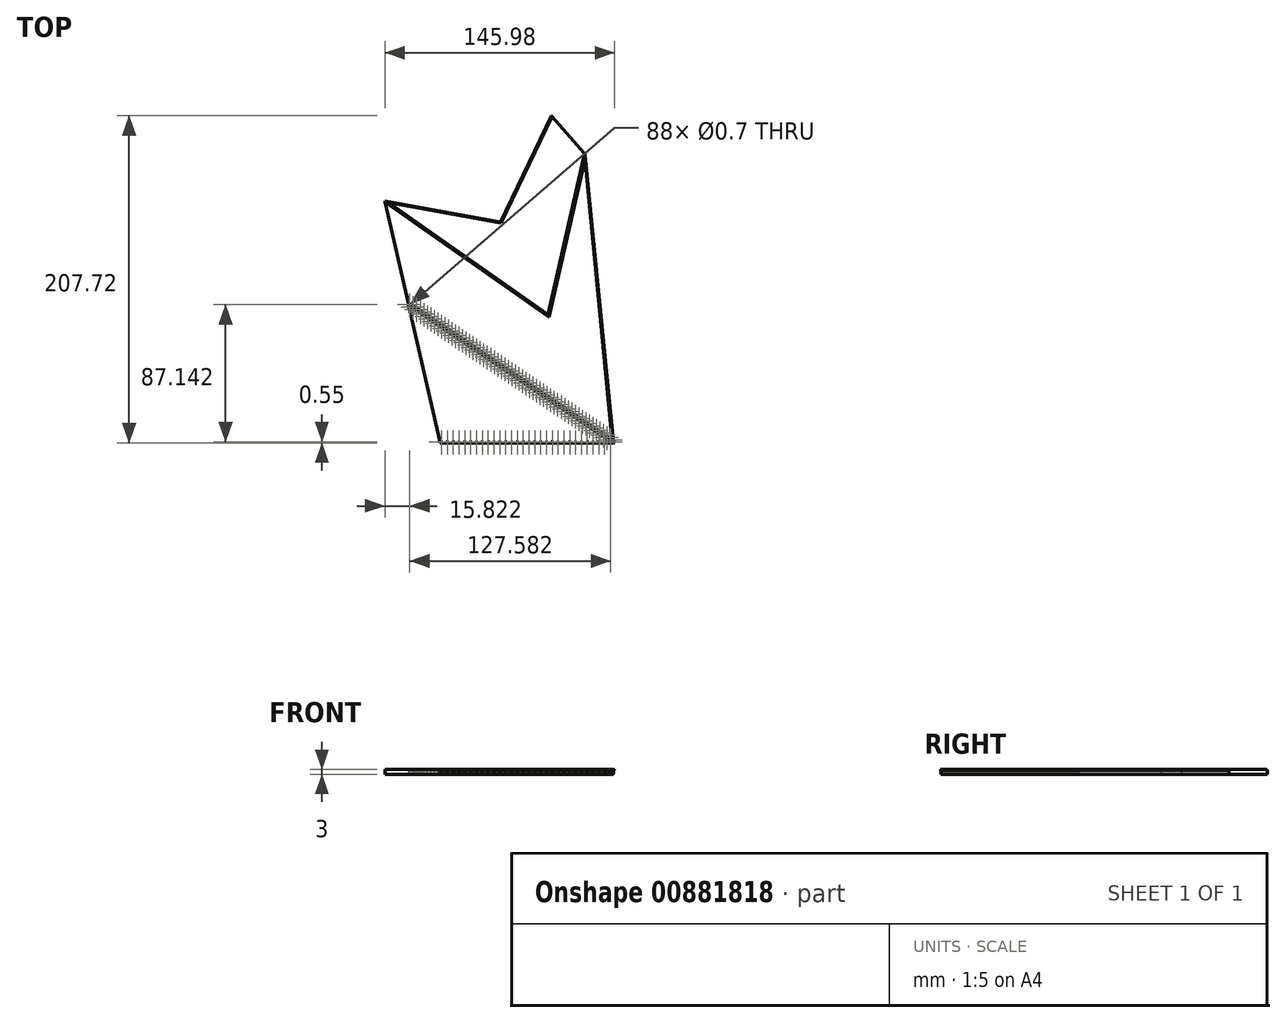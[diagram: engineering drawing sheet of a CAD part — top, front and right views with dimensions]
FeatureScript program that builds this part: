
annotation { "Feature Type Name" : "Feature", "Feature Type Description" : "" }
export const myFeature = defineFeature(function(context is Context, id is Id, definition is map)
    precondition{}
    {
        {
            var Q0;
            Q0=qCreatedBy(makeId("Top.planeOp"),FACE);
            var sketch = newSketch(context, id + "F0", { "sketchPlane" : qUnion([Q0])});
            skLineSegment(sketch, "E0", {"start": v(0, 0) * mm, "end": v(110, 0) * mm});
            skLineSegment(sketch, "E1", {"start": v(0, 0) * mm, "end": v(-20.1, 87.72) * mm});
            skLineSegment(sketch, "E2", {"start": v(-20.1, 87.72) * mm, "end": v(110, 0) * mm});
            skLineSegment(sketch, "E3", {"start": v(110, 0) * mm, "end": v(68.99, 80.11) * mm});
            skLineSegment(sketch, "E4", {"start": v(68.99, 80.11) * mm, "end": v(-20.1, 87.72) * mm});
            skLineSegment(sketch, "E5", {"start": v(-20.1, 87.72) * mm, "end": v(-35.08, 153.03) * mm});
            skLineSegment(sketch, "E6", {"start": v(-35.08, 153.03) * mm, "end": v(68.99, 80.11) * mm});
            skLineSegment(sketch, "E7", {"start": v(68.99, 80.11) * mm, "end": v(38.45, 139.75) * mm});
            skLineSegment(sketch, "E8", {"start": v(38.45, 139.75) * mm, "end": v(-35.08, 153.03) * mm});
            skPoint(sketch, "E9.center", {"position": v(55, -75.7) * mm});
            skLineSegment(sketch, "E10", {"start": v(68.99, 80.11) * mm, "end": v(97.55, 127.85) * mm});
            skLineSegment(sketch, "E11", {"start": v(38.45, 139.75) * mm, "end": v(70.67, 207.17) * mm});
            skLineSegment(sketch, "E12.MirrorCS", {"start": v(92.22, 182.65) * mm, "end": v(70.67, 207.17) * mm});
            skLineSegment(sketch, "E13", {"start": v(92.22, 182.65) * mm, "end": v(89.24, 213.26) * mm});
            skLineSegment(sketch, "E14", {"start": v(89.24, 213.26) * mm, "end": v(70.67, 207.17) * mm});
            skLineSegment(sketch, "E15", {"start": v(92.22, 182.65) * mm, "end": v(110, 0) * mm});
            skLineSegment(sketch, "E16", {"start": v(68.99, 80.11) * mm, "end": v(70.67, 207.17) * mm});
            skLineSegment(sketch, "E17", {"start": v(68.99, 80.11) * mm, "end": v(92.22, 182.65) * mm});
            skLineSegment(sketch, "E18", {"start": v(55, -75.7) * mm, "end": v(0, 0) * mm});
            skLineSegment(sketch, "E19", {"start": v(55, -75.7) * mm, "end": v(110, 0) * mm});
            skLineSegment(sketch, "E20", {"start": v(-20.1, 87.72) * mm, "end": v(-18.6, 105.36) * mm, "construction": true});
            skLineSegment(sketch, "E21", {"start": v(-18.6, 105.36) * mm, "end": v(-5.6, 104.24) * mm, "construction": true});
            skLineSegment(sketch, "E22", {"start": v(-20.1, 87.72) * mm, "end": v(-11.2, 100.93) * mm, "construction": true});
            skLineSegment(sketch, "E23", {"start": v(-11.2, 100.93) * mm, "end": v(-3.63, 95.82) * mm, "construction": true});
            skSolve(sketch);
        }
        {
            var Q0;
            Q0=qCreatedBy(makeId("Right.planeOp"),FACE);
            var sketch = newSketch(context, id + "F1", { "sketchPlane" : qUnion([Q0])});
            skLineSegment(sketch, "E24", {"start": v(0.55, 0) * mm, "end": v(-0.55, 0) * mm});
            skArc(sketch, "E25.MirrorCS", {"start": v(0.55, 0) * mm, "mid": v(0, -0.55) * mm, "end": v(-0.55, 0) * mm});
            skSolve(sketch);
        }
        {
            var Q0;
            Q0=makeQuery(id+"F1.imprint","IMPRINT",FACE,{"disambiguationData":[TD([[makeQuery(id+"F1.imprint","IMPRINT",EDGE,{"derivedFrom":sQuery(id+"F1.wireOp",EDGE,"E24")}),1.0]])]});
            var Q1;
            Q1=sQuery(id+"F0.wireOp",EDGE,"E0");
            var Q2;
            Q2=sQuery(id+"F0.wireOp",EDGE,"E3");
            var Q3;
            Q3=sQuery(id+"F0.wireOp",EDGE,"E7");
            sweep(context, id + "F2", {"profiles" : qUnion([Q0]), "path" : qUnion([Q1, Q2, Q3])});
        }
        {
            var Q0;
            Q0=sQuery(id+"F0.wireOp",EDGE,"E21");
            var Q1;
            Q1=sQuery(id+"F0.wireOp",VERTEX,"E1.end");
            cPlane(context, id + "F3", {"entities" : qUnion([Q0, Q1]), "cplaneType" : CPlaneType.LINE_POINT, "offset" : 25 * mm, "width" : 150 * mm, "height" : 150 * mm});
        }
        {
            var Q0;
            Q0=makeQuery(id+"F0.imprint","IMPRINT",FACE,{"disambiguationData":[TD([[makeQuery(id+"F0.imprint","IMPRINT",EDGE,{"derivedFrom":sQuery(id+"F0.wireOp",EDGE,"E0")}),-1.0]])]});
            var Q1;
            Q1=makeQuery(id+"F0.imprint","IMPRINT",FACE,{"disambiguationData":[TD([[makeQuery(id+"F0.imprint","IMPRINT",EDGE,{"derivedFrom":sQuery(id+"F0.wireOp",EDGE,"E1")}),-1.0]])]});
            var Q2;
            Q2=makeQuery(id+"F0.imprint","IMPRINT",FACE,{"disambiguationData":[TD([[makeQuery(id+"F0.imprint","IMPRINT",EDGE,{"derivedFrom":sQuery(id+"F0.wireOp",EDGE,"E2")}),1.0]])]});
            var Q3;
            Q3=makeQuery(id+"F0.imprint","IMPRINT",FACE,{"disambiguationData":[TD([[makeQuery(id+"F0.imprint","IMPRINT",EDGE,{"derivedFrom":sQuery(id+"F0.wireOp",EDGE,"E4")}),-1.0]])]});
            var Q4;
            Q4=makeQuery(id+"F0.imprint","IMPRINT",FACE,{"disambiguationData":[TD([[makeQuery(id+"F0.imprint","IMPRINT",EDGE,{"derivedFrom":sQuery(id+"F0.wireOp",EDGE,"E6")}),1.0]])]});
            var Q5;
            Q5=makeQuery(id+"F0.imprint","IMPRINT",FACE,{"disambiguationData":[TD([[makeQuery(id+"F0.imprint","IMPRINT",EDGE,{"derivedFrom":sQuery(id+"F0.wireOp",EDGE,"E7")}),-1.0]])]});
            var Q6;
            Q6=makeQuery(id+"F0.imprint","IMPRINT",FACE,{"disambiguationData":[TD([[makeQuery(id+"F0.imprint","IMPRINT",EDGE,{"derivedFrom":sQuery(id+"F0.wireOp",EDGE,"E12.MirrorCS")}),1.0]])]});
            var Q7;
            {var subQ0=sQuery(id+"F0.wireOp",EDGE,"E10");Q7=makeQuery(id+"F0.imprint","IMPRINT",FACE,{"disambiguationData":[TD([[makeQuery(id+"F0.imprint","IMPRINT",EDGE,{"derivedFrom":subQ0}),1.0]])]});}
            var Q8;
            {var subQ0=sQuery(id+"F0.wireOp",EDGE,"E3");Q8=makeQuery(id+"F0.imprint","IMPRINT",FACE,{"disambiguationData":[TD([[makeQuery(id+"F0.imprint","IMPRINT",EDGE,{"derivedFrom":subQ0}),-1.0]])]});}
            extrude(context, id + "F4", {"entities" : qUnion([Q0, Q1, Q2, Q3, Q4, Q5, Q6, Q7, Q8]), "operationType" : NewBodyOperationType.ADD, "oppositeDirection" : true, "depth" : 3 * mm, "offsetDistance" : 25 * mm});
        }
        {
            var Q0;
            Q0=sQuery(id+"F0.wireOp",EDGE,"E23");
            var Q1;
            Q1=sQuery(id+"F0.wireOp",VERTEX,"E1.end");
            cPlane(context, id + "F5", {"entities" : qUnion([Q0, Q1]), "cplaneType" : CPlaneType.LINE_POINT, "offset" : 25 * mm, "width" : 150 * mm, "height" : 150 * mm});
        }
        {
            var Q0;
            Q0=qCreatedBy(id+"F5.planeOp",FACE);
            var sketch = newSketch(context, id + "F6", { "sketchPlane" : qUnion([Q0])});
            skArc(sketch, "E26", {"start": v(60.94, 0) * mm, "mid": v(61.5, -0.55) * mm, "end": v(62.04, 0) * mm});
            skLineSegment(sketch, "E27", {"start": v(62.04, 0) * mm, "end": v(60.94, 0) * mm});
            skArc(sketch, "E28.MirrorCS", {"start": v(60.94, 0) * mm, "mid": v(61.5, 0.55) * mm, "end": v(62.04, 0) * mm});
            skSolve(sketch);
        }
        {
            var Q0;
            Q0=makeQuery(id+"F6.imprint","IMPRINT",FACE,{"disambiguationData":[TD([[makeQuery(id+"F6.imprint","IMPRINT",EDGE,{"derivedFrom":sQuery(id+"F6.wireOp",EDGE,"E26")}),1.0]])]});
            var Q1;
            Q1=sQuery(id+"F0.wireOp",EDGE,"E2");
            var Q2;
            Q2=sQuery(id+"F0.wireOp",EDGE,"E15");
            var Q3;
            Q3=sQuery(id+"F0.wireOp",EDGE,"E17");
            var Q4;
            Q4=sQuery(id+"F0.wireOp",EDGE,"E6");
            var Q5;
            Q5=sQuery(id+"F0.wireOp",EDGE,"E8");
            var Q6;
            Q6=sQuery(id+"F0.wireOp",EDGE,"E11");
            sweep(context, id + "F7", {"operationType" : NewBodyOperationType.REMOVE, "profiles" : qUnion([Q0]), "path" : qUnion([Q1, Q2, Q3, Q4, Q5, Q6])});
        }
        {
            var Q0;
            Q0=makeQuery(id+"F6.imprint","IMPRINT",FACE,{"disambiguationData":[TD([[makeQuery(id+"F6.imprint","IMPRINT",EDGE,{"derivedFrom":sQuery(id+"F6.wireOp",EDGE,"E27")}),-1.0]])]});
            var Q1;
            Q1=sQuery(id+"F0.wireOp",EDGE,"E2");
            sweep(context, id + "F8", {"operationType" : NewBodyOperationType.REMOVE, "profiles" : qUnion([Q0]), "path" : qUnion([Q1])});
        }
        {
            var Q0;
            Q0=qCreatedBy(makeId("Top.planeOp"),FACE);
            var sketch = newSketch(context, id + "F9", { "sketchPlane" : qUnion([Q0])});
            skCircle(sketch, "E29", {"center": v(0.99, 0) * mm, "radius": 0.35 * mm});
            skCircle(sketch, "E30.2.0.0", {"center": v(216.79, 0) * mm, "radius": 0.35 * mm});
            skCircle(sketch, "E30.3.0.0", {"center": v(324.69, 0) * mm, "radius": 0.35 * mm});
            skCircle(sketch, "E30.4.0.0", {"center": v(432.59, 0) * mm, "radius": 0.35 * mm});
            skCircle(sketch, "E31.1.0.0", {"center": v(4.69, 0) * mm, "radius": 0.35 * mm});
            skCircle(sketch, "E31.2.0.0", {"center": v(8.39, 0) * mm, "radius": 0.35 * mm});
            skCircle(sketch, "E31.3.0.0", {"center": v(12.09, 0) * mm, "radius": 0.35 * mm});
            skCircle(sketch, "E31.4.0.0", {"center": v(15.79, 0) * mm, "radius": 0.35 * mm});
            skCircle(sketch, "E31.5.0.0", {"center": v(19.49, 0) * mm, "radius": 0.35 * mm});
            skCircle(sketch, "E31.6.0.0", {"center": v(23.19, 0) * mm, "radius": 0.35 * mm});
            skCircle(sketch, "E31.7.0.0", {"center": v(26.89, 0) * mm, "radius": 0.35 * mm});
            skCircle(sketch, "E31.8.0.0", {"center": v(30.59, 0) * mm, "radius": 0.35 * mm});
            skCircle(sketch, "E31.9.0.0", {"center": v(34.29, 0) * mm, "radius": 0.35 * mm});
            skCircle(sketch, "E31.10.0.0", {"center": v(37.99, 0) * mm, "radius": 0.35 * mm});
            skCircle(sketch, "E31.11.0.0", {"center": v(41.69, 0) * mm, "radius": 0.35 * mm});
            skCircle(sketch, "E31.12.0.0", {"center": v(45.39, 0) * mm, "radius": 0.35 * mm});
            skCircle(sketch, "E31.13.0.0", {"center": v(49.09, 0) * mm, "radius": 0.35 * mm});
            skCircle(sketch, "E31.14.0.0", {"center": v(52.79, 0) * mm, "radius": 0.35 * mm});
            skCircle(sketch, "E31.15.0.0", {"center": v(56.49, 0) * mm, "radius": 0.35 * mm});
            skCircle(sketch, "E31.16.0.0", {"center": v(60.19, 0) * mm, "radius": 0.35 * mm});
            skCircle(sketch, "E31.17.0.0", {"center": v(63.89, 0) * mm, "radius": 0.35 * mm});
            skCircle(sketch, "E31.18.0.0", {"center": v(67.59, 0) * mm, "radius": 0.35 * mm});
            skCircle(sketch, "E31.19.0.0", {"center": v(71.29, 0) * mm, "radius": 0.35 * mm});
            skCircle(sketch, "E31.20.0.0", {"center": v(74.99, 0) * mm, "radius": 0.35 * mm});
            skCircle(sketch, "E31.21.0.0", {"center": v(78.69, 0) * mm, "radius": 0.35 * mm});
            skCircle(sketch, "E31.22.0.0", {"center": v(82.39, 0) * mm, "radius": 0.35 * mm});
            skCircle(sketch, "E31.23.0.0", {"center": v(86.09, 0) * mm, "radius": 0.35 * mm});
            skCircle(sketch, "E31.24.0.0", {"center": v(89.79, 0) * mm, "radius": 0.35 * mm});
            skCircle(sketch, "E31.25.0.0", {"center": v(93.49, 0) * mm, "radius": 0.35 * mm});
            skCircle(sketch, "E31.26.0.0", {"center": v(97.19, 0) * mm, "radius": 0.35 * mm});
            skCircle(sketch, "E31.27.0.0", {"center": v(100.89, 0) * mm, "radius": 0.35 * mm});
            skCircle(sketch, "E31.28.0.0", {"center": v(104.59, 0) * mm, "radius": 0.35 * mm});
            skCircle(sketch, "E31.29.0.0", {"center": v(108.29, 0) * mm, "radius": 0.35 * mm});
            skLineSegment(sketch, "E31.direction1", {"start": v(0.99, 0) * mm, "end": v(4.69, 0) * mm, "construction": true});
            skCircle(sketch, "E32", {"center": v(-19.26, 87.14) * mm, "radius": 0.35 * mm});
            skCircle(sketch, "E33.1.0.0", {"center": v(-17.02, 85.63) * mm, "radius": 0.35 * mm});
            skCircle(sketch, "E33.2.0.0", {"center": v(-14.78, 84.13) * mm, "radius": 0.35 * mm});
            skCircle(sketch, "E33.3.0.0", {"center": v(-12.54, 82.62) * mm, "radius": 0.35 * mm});
            skCircle(sketch, "E33.4.0.0", {"center": v(-10.3, 81.11) * mm, "radius": 0.35 * mm});
            skCircle(sketch, "E33.5.0.0", {"center": v(-8.07, 79.6) * mm, "radius": 0.35 * mm});
            skCircle(sketch, "E33.6.0.0", {"center": v(-5.83, 78.1) * mm, "radius": 0.35 * mm});
            skCircle(sketch, "E33.7.0.0", {"center": v(-3.59, 76.59) * mm, "radius": 0.35 * mm});
            skCircle(sketch, "E33.8.0.0", {"center": v(-1.35, 75.08) * mm, "radius": 0.35 * mm});
            skCircle(sketch, "E33.9.0.0", {"center": v(0.89, 73.57) * mm, "radius": 0.35 * mm});
            skCircle(sketch, "E33.10.0.0", {"center": v(3.13, 72.07) * mm, "radius": 0.35 * mm});
            skCircle(sketch, "E33.11.0.0", {"center": v(5.36, 70.56) * mm, "radius": 0.35 * mm});
            skCircle(sketch, "E33.12.0.0", {"center": v(7.6, 69.05) * mm, "radius": 0.35 * mm});
            skCircle(sketch, "E33.13.0.0", {"center": v(9.84, 67.54) * mm, "radius": 0.35 * mm});
            skCircle(sketch, "E33.14.0.0", {"center": v(12.08, 66.04) * mm, "radius": 0.35 * mm});
            skCircle(sketch, "E33.15.0.0", {"center": v(14.32, 64.53) * mm, "radius": 0.35 * mm});
            skCircle(sketch, "E33.16.0.0", {"center": v(16.56, 63.02) * mm, "radius": 0.35 * mm});
            skCircle(sketch, "E33.17.0.0", {"center": v(18.8, 61.51) * mm, "radius": 0.35 * mm});
            skCircle(sketch, "E33.18.0.0", {"center": v(21.03, 60) * mm, "radius": 0.35 * mm});
            skCircle(sketch, "E33.19.0.0", {"center": v(23.27, 58.5) * mm, "radius": 0.35 * mm});
            skCircle(sketch, "E33.20.0.0", {"center": v(25.5, 57) * mm, "radius": 0.35 * mm});
            skCircle(sketch, "E33.21.0.0", {"center": v(27.75, 55.48) * mm, "radius": 0.35 * mm});
            skCircle(sketch, "E33.22.0.0", {"center": v(29.98, 53.98) * mm, "radius": 0.35 * mm});
            skCircle(sketch, "E33.23.0.0", {"center": v(32.22, 52.47) * mm, "radius": 0.35 * mm});
            skCircle(sketch, "E33.24.0.0", {"center": v(34.46, 50.96) * mm, "radius": 0.35 * mm});
            skCircle(sketch, "E33.25.0.0", {"center": v(36.7, 49.45) * mm, "radius": 0.35 * mm});
            skCircle(sketch, "E33.26.0.0", {"center": v(38.94, 47.95) * mm, "radius": 0.35 * mm});
            skCircle(sketch, "E33.27.0.0", {"center": v(41.18, 46.44) * mm, "radius": 0.35 * mm});
            skCircle(sketch, "E33.28.0.0", {"center": v(43.41, 44.93) * mm, "radius": 0.35 * mm});
            skCircle(sketch, "E33.29.0.0", {"center": v(45.65, 43.42) * mm, "radius": 0.35 * mm});
            skCircle(sketch, "E33.30.0.0", {"center": v(47.9, 41.91) * mm, "radius": 0.35 * mm});
            skCircle(sketch, "E33.31.0.0", {"center": v(50.13, 40.4) * mm, "radius": 0.35 * mm});
            skCircle(sketch, "E33.32.0.0", {"center": v(52.37, 38.9) * mm, "radius": 0.35 * mm});
            skCircle(sketch, "E33.33.0.0", {"center": v(54.6, 37.4) * mm, "radius": 0.35 * mm});
            skCircle(sketch, "E33.34.0.0", {"center": v(56.84, 35.88) * mm, "radius": 0.35 * mm});
            skCircle(sketch, "E33.35.0.0", {"center": v(59.08, 34.38) * mm, "radius": 0.35 * mm});
            skCircle(sketch, "E33.36.0.0", {"center": v(61.32, 32.87) * mm, "radius": 0.35 * mm});
            skCircle(sketch, "E33.37.0.0", {"center": v(63.56, 31.36) * mm, "radius": 0.35 * mm});
            skCircle(sketch, "E33.38.0.0", {"center": v(65.8, 29.85) * mm, "radius": 0.35 * mm});
            skCircle(sketch, "E33.39.0.0", {"center": v(68.04, 28.35) * mm, "radius": 0.35 * mm});
            skCircle(sketch, "E33.40.0.0", {"center": v(70.27, 26.84) * mm, "radius": 0.35 * mm});
            skCircle(sketch, "E33.41.0.0", {"center": v(72.51, 25.33) * mm, "radius": 0.35 * mm});
            skCircle(sketch, "E33.42.0.0", {"center": v(74.75, 23.82) * mm, "radius": 0.35 * mm});
            skCircle(sketch, "E33.43.0.0", {"center": v(76.99, 22.32) * mm, "radius": 0.35 * mm});
            skCircle(sketch, "E33.44.0.0", {"center": v(79.23, 20.8) * mm, "radius": 0.35 * mm});
            skCircle(sketch, "E33.45.0.0", {"center": v(81.47, 19.3) * mm, "radius": 0.35 * mm});
            skCircle(sketch, "E33.46.0.0", {"center": v(83.7, 17.8) * mm, "radius": 0.35 * mm});
            skCircle(sketch, "E33.47.0.0", {"center": v(85.94, 16.29) * mm, "radius": 0.35 * mm});
            skCircle(sketch, "E33.48.0.0", {"center": v(88.18, 14.78) * mm, "radius": 0.35 * mm});
            skCircle(sketch, "E33.49.0.0", {"center": v(90.42, 13.27) * mm, "radius": 0.35 * mm});
            skCircle(sketch, "E33.50.0.0", {"center": v(92.66, 11.76) * mm, "radius": 0.35 * mm});
            skCircle(sketch, "E33.51.0.0", {"center": v(94.9, 10.26) * mm, "radius": 0.35 * mm});
            skCircle(sketch, "E33.52.0.0", {"center": v(97.13, 8.75) * mm, "radius": 0.35 * mm});
            skCircle(sketch, "E33.53.0.0", {"center": v(99.37, 7.24) * mm, "radius": 0.35 * mm});
            skCircle(sketch, "E33.54.0.0", {"center": v(101.61, 5.73) * mm, "radius": 0.35 * mm});
            skCircle(sketch, "E33.55.0.0", {"center": v(103.85, 4.23) * mm, "radius": 0.35 * mm});
            skCircle(sketch, "E33.56.0.0", {"center": v(106.09, 2.72) * mm, "radius": 0.35 * mm});
            skCircle(sketch, "E33.57.0.0", {"center": v(108.32, 1.21) * mm, "radius": 0.35 * mm});
            skLineSegment(sketch, "E33.direction1", {"start": v(-19.26, 87.14) * mm, "end": v(-17.02, 85.63) * mm, "construction": true});
            skSolve(sketch);
        }
        {
            var Q0;
            Q0 = qSketchRegion(id + "F9", true);
            extrude(context, id + "F10", {"entities" : qUnion([Q0]), "operationType" : NewBodyOperationType.REMOVE, "oppositeDirection" : true, "depth" : 25 * mm, "offsetDistance" : 25 * mm, "hasSecondDirection" : true, "secondDirectionOppositeDirection" : false, "secondDirectionDepth" : 25 * mm});
        }
    });
